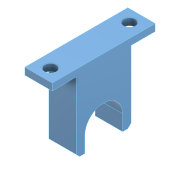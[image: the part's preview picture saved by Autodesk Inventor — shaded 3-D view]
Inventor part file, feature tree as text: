
AUTODESK INVENTOR PART (.ipt)
format: ipt  version: 2022 (Build 260153000, 153)  size: 140,800 bytes
history: native  units: mm
features: sketch x3, extrude x2, hole x1, chamfer x1, projected_geometry x1
ambient origin geometry x8: Origin, YZ Plane, XZ Plane, XY Plane, X Axis, Y Axis, Z Axis, Center Point
bodies: Solid1 (feature_tree)
feature tree (8):
  extrude  "Extrusion1"  Depth=2.5mm
  extrude  "Extrusion2"  Depth=18.0mm
  hole  "Hole1"  [1 undecoded]
  chamfer  "Chamfer1"  Distance=2.0mm
  sketch  "Sketch2"  dims[d2=2.5mm d3=9.0mm]
  sketch  "Sketch3"  dims[d4=1.0mm d5=18.0mm]
  sketch  "Sketch4"  dims[d6=8.0mm d7=0.0mm d8=7.0mm d9=2.0mm d10=0.0mm d11=3.4mm d12=6.0mm d13=6.0mm d14=2.0mm d15=90.0deg d16=8.0mm d17=20.594885mm d18=4.5mm d19=1.0mm d20=2.0mm d21=45.0deg]
  projected_geometry  "Project Cut Edges1"
note: 1 required parameter value undecoded (feature->parameter linkage not recoverable at this tier; creation-order binding heuristic only, values carry confidence <= 0.55)
